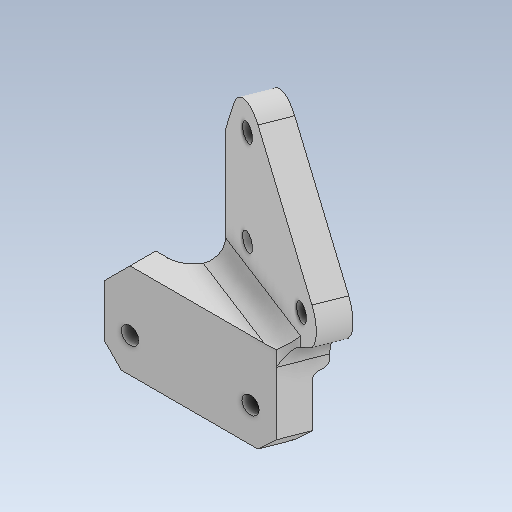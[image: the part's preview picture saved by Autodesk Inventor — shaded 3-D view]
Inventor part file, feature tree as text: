
AUTODESK INVENTOR PART (.ipt)
format: ipt  version: 2023 (Build 270158000, 158)  size: 187,392 bytes
history: native  units: mm
features: sketch x9, other x3
ambient origin geometry x8: Origin, YZ Plane, XZ Plane, XY Plane, X Axis, Y Axis, Z Axis, Center Point
bodies: Solid1 (feature_tree)
feature tree (12):
  other  "body_conn_1.ipt"
  other  "Solid1::body_conn_1.ipt"
  other  "TaggingFeature1"
  sketch  "Sketch1"  dims[d0=10.0mm]
  sketch  "Sketch2"
  sketch  "Sketch3"
  sketch  "Sketch4"
  sketch  "Sketch5"
  sketch  "Sketch6"
  sketch  "Sketch7"
  sketch  "Sketch8"
  sketch  "Sketch9"
